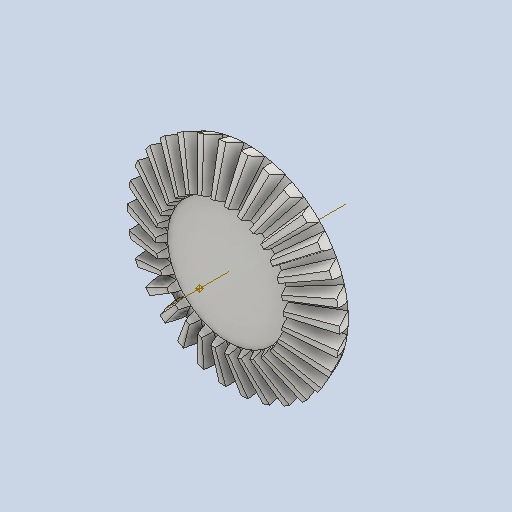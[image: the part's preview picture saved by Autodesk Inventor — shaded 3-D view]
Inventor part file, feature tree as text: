
AUTODESK INVENTOR PART (.ipt)
format: ipt  version: 2022 (Build 260153000, 153)  size: 624,640 bytes
history: native  units: mm
features: other x24, loft x2, pattern_circular x2, sketch x1
ambient origin geometry x6: Origin, XZ Plane, X Axis, Y Axis, Z Axis, Center Point
bodies: Solid1 (feature_tree)
feature tree (29):
  other  "Top Point"
  other  "Mesh Plane2"
  other  "Teeth Body"
  other  "Start Point"
  other  "Tooth Plane"
  other  "Start Sketch"
  other  "End Point"
  other  "3D Sketch Right"
  other  "End Plane Right"
  loft  "Loft Right"
  pattern_circular  "Circular Pattern Right"  [2 undecoded]
  other  "3D Sketch Left"
  other  "End Plane Left"
  loft  "Loft Left"
  pattern_circular  "Circular Pattern Left"  [2 undecoded]
  other  "Fix Body"
  other  "Mesh Plane"
  other  "Top Plane"
  other  "Teeth Body Sketch"
  other  "End Plane"
  other  "End Sketch"
  other  "Helical Curve Left"
  other  "End Sketch Left"
  other  "Body Sketch"
  sketch  "Sketch6"  dims[d0=60.0mm d1=58.217325mm d2=61.485563mm d3=12.9mm d4=10.143047mm d5=90.0deg d7=21.163271mm d8=21.961152mm d9=75.095331mm d11=13.12mm d12=12.569844mm d15=13.043742mm d16=44.602586mm d17=0.0mm d18=90.0deg d19=0.0mm d20=90.0deg d21=300.0mm d22=360.0deg d26=153.943419mm d27=4.872646mm d28=60.0mm d29=-11.902899mm d30=12.569844mm d31=13.043742mm d32=44.602586mm d35=0.0mm d37=0.0mm d39=0.0mm d40=90.0deg d41=300.0mm d42=360.0deg d46=90.0deg d47=90.0deg d48=0.0mm d49=0.0mm d50=90.0deg d51=1.047198mm d52=0.0mm d53=0.0mm d54=0.0mm d56=6.915476mm d57=84.097472mm d58=77.849472mm d59=49.949373mm d60=46.238397mm d61=49.949373mm d62=46.238397mm d63=90.0deg d64=90.0deg d65=153.943419mm d66=31.5mm d67=60.0mm d68=-11.902899mm d69=4.872646mm d70=13.043742mm d71=44.602586mm d72=12.569844mm d73=46.238397mm d74=49.949373mm d75=0.0mm d76=90.0deg d77=0.0mm d78=90.0deg d79=0.0mm d80=90.0deg d81=300.0mm d82=360.0deg d84=10.0mm d85=20.0mm d86=20.0mm d87=10.0mm d88=0.0mm d89=0.0mm]
  other  "Srf1"
  other  "Helical Curve Right"
  other  "End Sketch Right"
  other  "Pitch Diameter"
note: 4 required parameter values undecoded (feature->parameter linkage not recoverable at this tier; creation-order binding heuristic only, values carry confidence <= 0.55)
